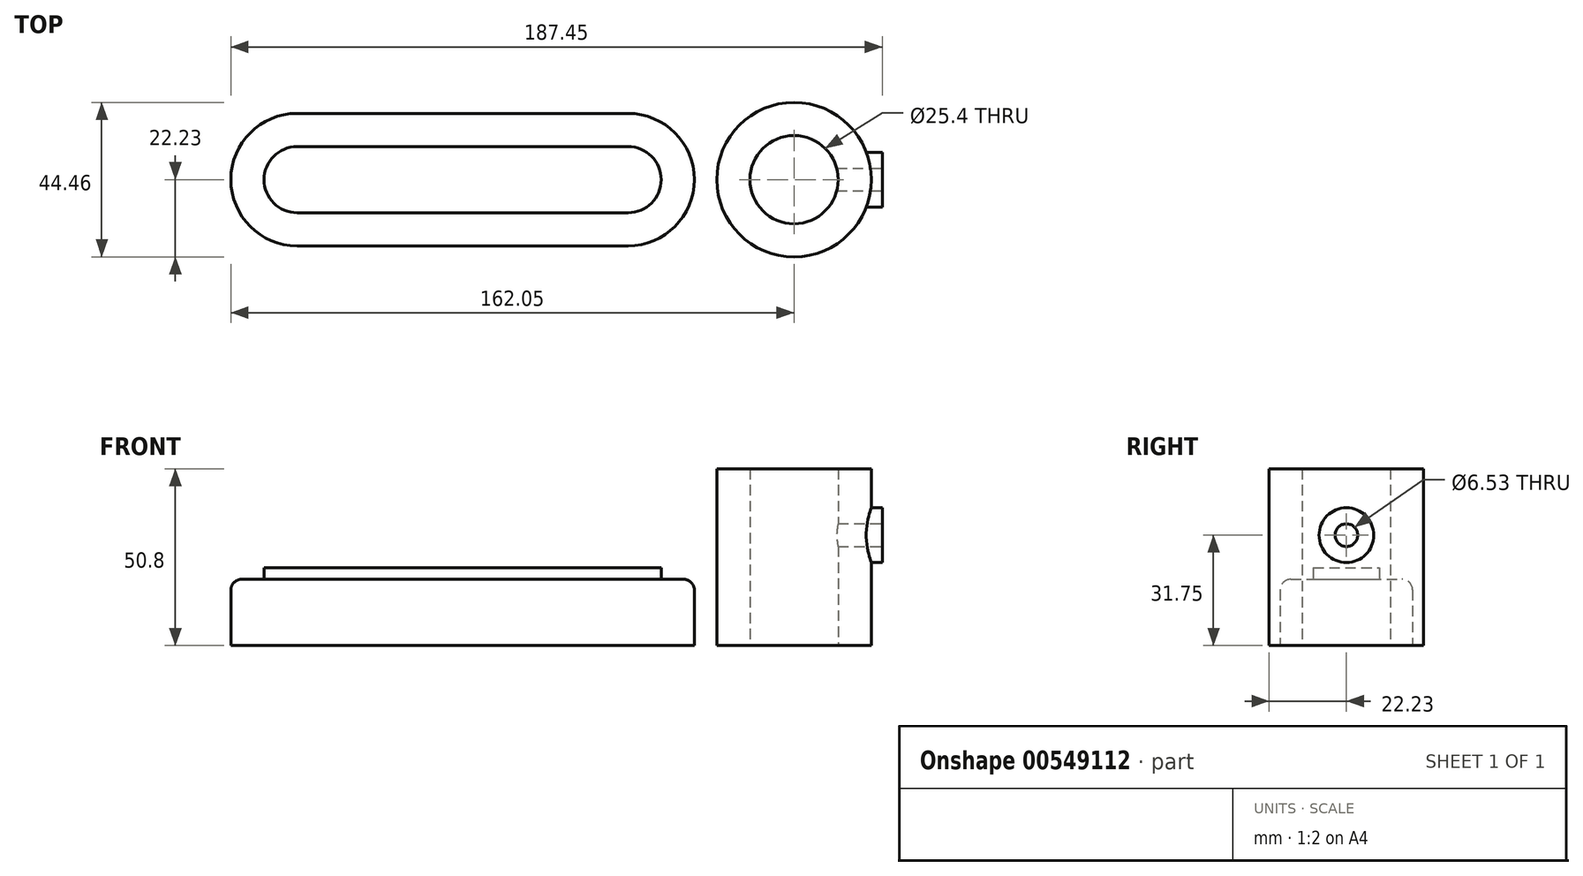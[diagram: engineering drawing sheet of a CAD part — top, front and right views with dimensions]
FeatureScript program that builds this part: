
annotation { "Feature Type Name" : "Feature", "Feature Type Description" : "" }
export const myFeature = defineFeature(function(context is Context, id is Id, definition is map)
    precondition{}
    {
        {
            var Q0;
            Q0=qCreatedBy(makeId("Top.planeOp"),FACE);
            var sketch = newSketch(context, id + "F0", { "sketchPlane" : qUnion([Q0])});
            skCircle(sketch, "E0", {"center": v(0, 0) * mm, "radius": 22.23 * mm});
            skCircle(sketch, "E1", {"center": v(0, 0) * mm, "radius": 12.7 * mm});
            skLineSegment(sketch, "E2", {"start": v(-47.75, 0) * mm, "end": v(-143, 0) * mm, "construction": true});
            skArc(sketch, "E3.0.startCap", {"start": v(-47.75, 9.53) * mm, "mid": v(-38.23, 0) * mm, "end": v(-47.75, -9.53) * mm});
            skArc(sketch, "E3.0.endCap", {"start": v(-143, -9.53) * mm, "mid": v(-152.53, 0) * mm, "end": v(-143, 9.53) * mm});
            skLineSegment(sketch, "E3.0.left", {"start": v(-47.75, -9.53) * mm, "end": v(-143, -9.53) * mm});
            skLineSegment(sketch, "E3.0.right", {"start": v(-47.75, 9.53) * mm, "end": v(-143, 9.53) * mm});
            skArc(sketch, "E4.0.startCap", {"start": v(-47.75, 19.05) * mm, "mid": v(-28.7, 0) * mm, "end": v(-47.75, -19.05) * mm});
            skArc(sketch, "E4.0.endCap", {"start": v(-143, -19.05) * mm, "mid": v(-162.05, 0) * mm, "end": v(-143, 19.05) * mm});
            skLineSegment(sketch, "E4.0.left", {"start": v(-47.75, -19.05) * mm, "end": v(-143, -19.05) * mm});
            skLineSegment(sketch, "E4.0.right", {"start": v(-47.75, 19.05) * mm, "end": v(-143, 19.05) * mm});
            skArc(sketch, "E5.0.startCap", {"start": v(-47.75, 27.3) * mm, "mid": v(-40.87, 26.42) * mm, "end": v(-34.44, 23.84) * mm});
            skArc(sketch, "E5.0.endCap", {"start": v(-143, -27.3) * mm, "mid": v(-170.3, 0) * mm, "end": v(-143, 27.3) * mm});
            skLineSegment(sketch, "E5.0.left", {"start": v(-47.75, -27.3) * mm, "end": v(-143, -27.3) * mm});
            skLineSegment(sketch, "E5.0.right", {"start": v(-47.75, 27.3) * mm, "end": v(-143, 27.3) * mm});
            skLineSegment(sketch, "E6", {"start": v(0, 22.23) * mm, "end": v(-28.24, 22.23) * mm});
            skLineSegment(sketch, "E7", {"start": v(0, -22.23) * mm, "end": v(-28.24, -22.23) * mm});
            skArc(sketch, "E8.trimOffspring", {"start": v(-34.44, -23.84) * mm, "mid": v(-40.87, -26.42) * mm, "end": v(-47.75, -27.3) * mm});
            skPoint(sketch, "E9.visualSharp", {"position": v(-31.89, 22.22) * mm});
            skArc(sketch, "E9.filletArc", {"start": v(-34.44, 23.84) * mm, "mid": v(-31.44, 22.63) * mm, "end": v(-28.24, 22.23) * mm});
            skPoint(sketch, "E10.visualSharp", {"position": v(-31.89, -22.23) * mm});
            skArc(sketch, "E10.filletArc", {"start": v(-28.24, -22.23) * mm, "mid": v(-31.44, -22.63) * mm, "end": v(-34.44, -23.84) * mm});
            skSolve(sketch);
        }
        {
            var Q0;
            Q0=makeQuery(id+"F0.imprint","IMPRINT",FACE,{"disambiguationData":[TD([[makeQuery(id+"F0.imprint","IMPRINT",EDGE,{"derivedFrom":sQuery(id+"F0.wireOp",EDGE,"E1")}),-1.0]])]});
            extrude(context, id + "F1", {"entities" : qUnion([Q0]), "depth" : 50.8 * mm, "offsetDistance" : 25.4 * mm});
        }
        {
            var Q0;
            Q0=makeQuery(id+"F0.imprint","IMPRINT",FACE,{"disambiguationData":[TD([[makeQuery(id+"F0.imprint","IMPRINT",EDGE,{"derivedFrom":sQuery(id+"F0.wireOp",EDGE,"E4.0.startCap")}),1.0]])]});
            extrude(context, id + "F2", {"entities" : qUnion([Q0]), "operationType" : NewBodyOperationType.ADD, "depth" : 19.05 * mm, "offsetDistance" : 25.4 * mm});
        }
        {
            var Q0;
            Q0=makeQuery(id+"F0.imprint","IMPRINT",FACE,{"disambiguationData":[TD([[makeQuery(id+"F0.imprint","IMPRINT",EDGE,{"derivedFrom":sQuery(id+"F0.wireOp",EDGE,"E3.0.startCap")}),1.0]])]});
            extrude(context, id + "F3", {"entities" : qUnion([Q0]), "operationType" : NewBodyOperationType.ADD, "depth" : 22.35 * mm, "offsetDistance" : 25.4 * mm});
        }
        {
            var Q0;
            Q0=makeQuery(id+"F2.opExtrude","CAP_EDGE",EDGE,{"disambiguationData":[OSD([sQuery(id+"F0.wireOp",EDGE,"E4.0.left")])],"isStart":false});
            var Q1;
            Q1=makeQuery(id+"F2.opExtrude","CAP_EDGE",EDGE,{"disambiguationData":[OSD([sQuery(id+"F0.wireOp",EDGE,"E5.0.left")])],"isStart":false});
            var Q2;
            Q2=makeQuery(id+"F2.opExtrude","CAP_EDGE",EDGE,{"disambiguationData":[OSD([sQuery(id+"F0.wireOp",EDGE,"E0")])],"isStart":false});
            fillet(context, id + "F4", {"entities" : qUnion([Q0, Q1, Q2]), "radius" : 3.05 * mm, "tangentPropagation" : true, "allowEdgeOverflow" : false});
        }
        {
            var Q0;
            Q0=qCreatedBy(makeId("Right.planeOp"),FACE);
            cPlane(context, id + "F5", {"entities" : qUnion([Q0]), "cplaneType" : CPlaneType.OFFSET, "offset" : 25.4 * mm, "width" : 152.4 * mm, "height" : 152.4 * mm});
        }
        {
            var Q0;
            Q0=qCreatedBy(id+"F5.planeOp",FACE);
            var sketch = newSketch(context, id + "F6", { "sketchPlane" : qUnion([Q0])});
            skCircle(sketch, "E11", {"center": v(0, 31.75) * mm, "radius": 7.87 * mm});
            skCircle(sketch, "E12", {"center": v(0, 31.75) * mm, "radius": 3.26 * mm});
            skSolve(sketch);
        }
        {
            var Q0;
            Q0=makeQuery(id+"F6.imprint","IMPRINT",FACE,{"disambiguationData":[TD([[makeQuery(id+"F6.imprint","IMPRINT",EDGE,{"derivedFrom":sQuery(id+"F6.wireOp",EDGE,"E11")}),1.0]])]});
            var Q1;
            Q1=sQuery(id+"F6.wireOp",EDGE,"E11");
            extrude(context, id + "F7", {"entities" : qUnion([Q0]), "operationType" : NewBodyOperationType.ADD, "surfaceEntities" : qUnion([Q1]), "endBound" : BoundingType.UP_TO_NEXT, "oppositeDirection" : true, "depth" : 25.4 * mm, "offsetDistance" : 25.4 * mm});
        }
        {
            var Q0;
            Q0=sQuery(id+"F6.wireOp",VERTEX,"E11.center");
            var Q1;
            Q1=makeQuery(id+"F1.opExtrude","SWEPT_BODY",BODY,{"disambiguationData":[OSD([sQuery(id+"F0.wireOp",EDGE,"E0"),sQuery(id+"F0.wireOp",EDGE,"E1")])]});
            hole(context, id + "F8", {"style" : HoleStyle.SIMPLE, "endStyle" : HoleEndStyle.BLIND, "holeDiameter" : 6.53 * mm, "majorDiameter" : 6.35 * mm, "holeDepth" : 25.4 * mm, "isTappedThrough" : true, "tappedDepth" : 12.7 * mm, "tapClearance" : 3, "locations" : qUnion([Q0]), "scope" : qUnion([Q1])});
        }
    });
